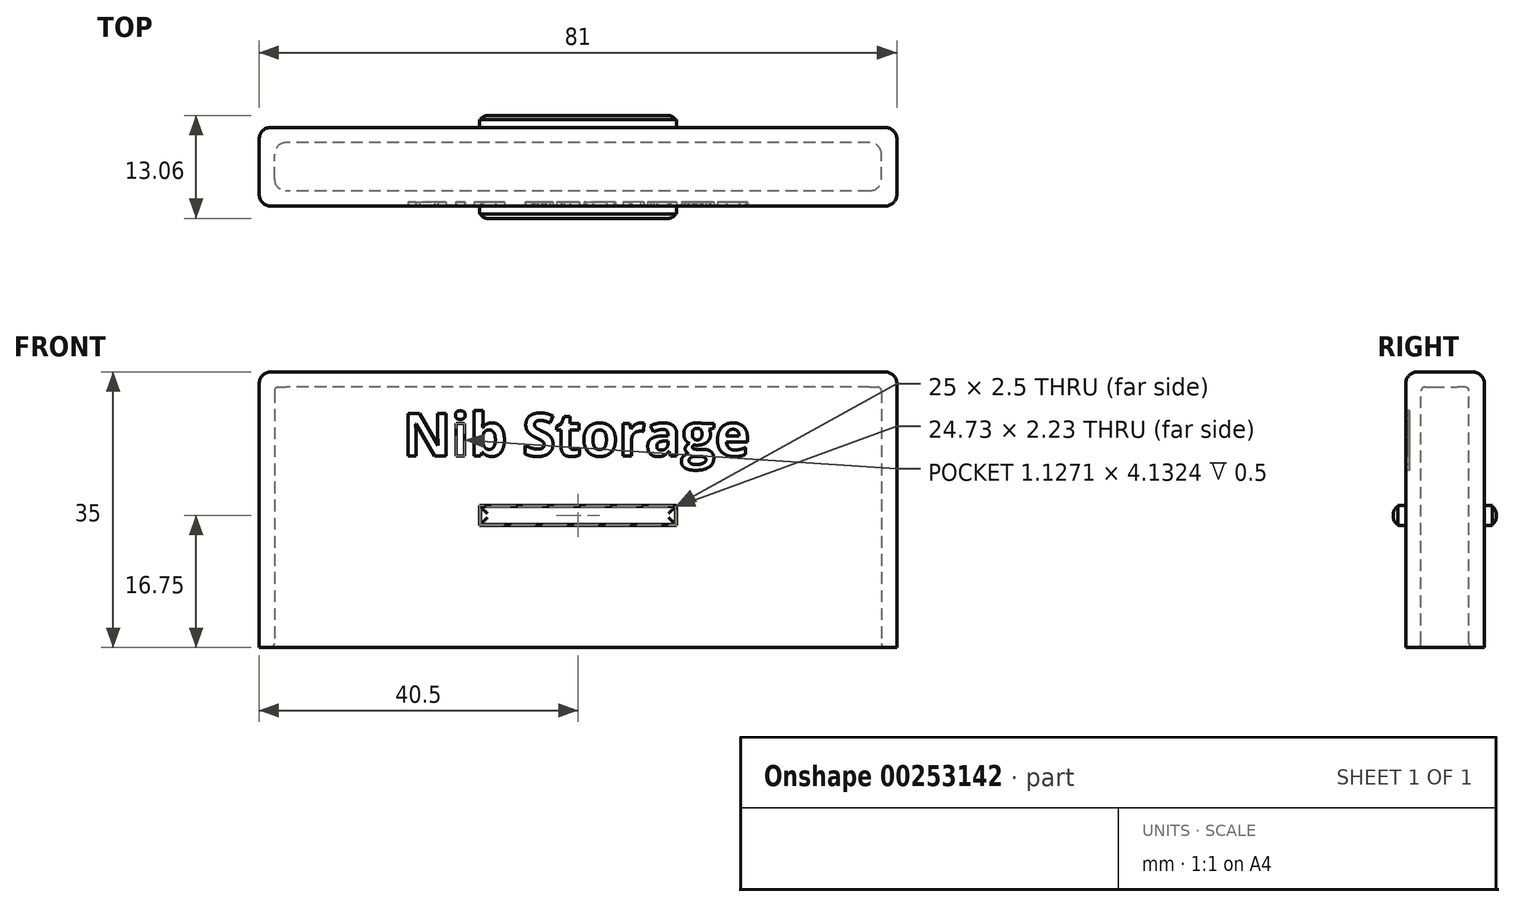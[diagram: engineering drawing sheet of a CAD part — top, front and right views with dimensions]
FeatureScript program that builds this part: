
annotation { "Feature Type Name" : "Feature", "Feature Type Description" : "" }
export const myFeature = defineFeature(function(context is Context, id is Id, definition is map)
    precondition{}
    {
        {
            var Q0;
            Q0=qCreatedBy(makeId("Top.planeOp"),FACE);
            var sketch = newSketch(context, id + "F0", { "sketchPlane" : qUnion([Q0])});
            skLineSegment(sketch, "E0.bottom", {"start": v(40.5, -5) * mm, "end": v(-40.5, -5) * mm});
            skLineSegment(sketch, "E0.top", {"start": v(40.5, 5) * mm, "end": v(-40.5, 5) * mm});
            skLineSegment(sketch, "E0.left", {"start": v(40.5, -5) * mm, "end": v(40.5, 5) * mm});
            skLineSegment(sketch, "E0.right", {"start": v(-40.5, -5) * mm, "end": v(-40.5, 5) * mm});
            skPoint(sketch, "E0.middle", {"position": v(0, 0) * mm});
            skSolve(sketch);
        }
        {
            var Q0;
            Q0=qSketchRegion(id+"F0",true);
            extrude(context, id + "F1", {"entities" : qUnion([Q0]), "depth" : 35 * mm});
        }
        {
            var Q0;
            Q0=makeQuery(id+"F1.opExtrude","CAP_EDGE",EDGE,{"disambiguationData":[OSD([sQuery(id+"F0.wireOp",EDGE,"E0.top")])],"isStart":false});
            var Q1;
            Q1=makeQuery(id+"F1.opExtrude","CAP_EDGE",EDGE,{"disambiguationData":[OSD([sQuery(id+"F0.wireOp",EDGE,"E0.bottom")])],"isStart":false});
            var Q2;
            Q2=makeQuery(id+"F1.opExtrude","CAP_EDGE",EDGE,{"disambiguationData":[OSD([sQuery(id+"F0.wireOp",EDGE,"E0.right")])],"isStart":false});
            var Q3;
            Q3=makeQuery(id+"F1.opExtrude","CAP_EDGE",EDGE,{"disambiguationData":[OSD([sQuery(id+"F0.wireOp",EDGE,"E0.left")])],"isStart":false});
            var Q4;
            Q4=makeQuery(id+"F1.opExtrude","SWEPT_EDGE",EDGE,{"disambiguationData":[OSD([sQuery(id+"F0.wireOp",EDGE,"E0.top"),sQuery(id+"F0.wireOp",EDGE,"E0.right")])]});
            var Q5;
            Q5=makeQuery(id+"F1.opExtrude","SWEPT_EDGE",EDGE,{"disambiguationData":[OSD([sQuery(id+"F0.wireOp",EDGE,"E0.bottom"),sQuery(id+"F0.wireOp",EDGE,"E0.right")])]});
            var Q6;
            Q6=makeQuery(id+"F1.opExtrude","SWEPT_EDGE",EDGE,{"disambiguationData":[OSD([sQuery(id+"F0.wireOp",EDGE,"E0.top"),sQuery(id+"F0.wireOp",EDGE,"E0.left")])]});
            var Q7;
            Q7=makeQuery(id+"F1.opExtrude","SWEPT_EDGE",EDGE,{"disambiguationData":[OSD([sQuery(id+"F0.wireOp",EDGE,"E0.bottom"),sQuery(id+"F0.wireOp",EDGE,"E0.left")])]});
            fillet(context, id + "F2", {"entities" : qUnion([Q0, Q1, Q2, Q3, Q4, Q5, Q6, Q7]), "radius" : 1.5 * mm, "tangentPropagation" : true, "allowEdgeOverflow" : false});
        }
        {
            var Q0;
            Q0=makeQuery(id+"F1.opExtrude","CAP_FACE",FACE,{"disambiguationData":[OSD([sQuery(id+"F0.wireOp",EDGE,"E0.bottom"),sQuery(id+"F0.wireOp",EDGE,"E0.top"),sQuery(id+"F0.wireOp",EDGE,"E0.left"),sQuery(id+"F0.wireOp",EDGE,"E0.right")])],"isStart":true});
            shell(context, id + "F3", {"entities" : qUnion([Q0]), "thickness" : 1.94 * mm});
        }
        {
            var Q0;
            Q0=makeQuery(id+"F3.opShell","OFFSET_EDGE",EDGE,{"disambiguationData":[OSD([sQuery(id+"F0.wireOp",EDGE,"E0.top"),sQuery(id+"F0.wireOp",EDGE,"E0.left")])]});
            var Q1;
            Q1=makeQuery(id+"F3.opShell","OFFSET_EDGE",EDGE,{"disambiguationData":[OSD([sQuery(id+"F0.wireOp",EDGE,"E0.bottom"),sQuery(id+"F0.wireOp",EDGE,"E0.left")])]});
            var Q2;
            Q2=makeQuery(id+"F3.opShell","OFFSET_EDGE",EDGE,{"disambiguationData":[OSD([sQuery(id+"F0.wireOp",EDGE,"E0.bottom"),sQuery(id+"F0.wireOp",EDGE,"E0.right")])]});
            var Q3;
            Q3=makeQuery(id+"F3.opShell","OFFSET_EDGE",EDGE,{"disambiguationData":[OSD([sQuery(id+"F0.wireOp",EDGE,"E0.top"),sQuery(id+"F0.wireOp",EDGE,"E0.right")])]});
            fillet(context, id + "F4", {"entities" : qUnion([Q0, Q1, Q2, Q3]), "radius" : 1.5 * mm, "tangentPropagation" : true, "allowEdgeOverflow" : false});
        }
        {
            var Q0;
            Q0=makeQuery(id+"F1.opExtrude","SWEPT_FACE",FACE,{"disambiguationData":[OSD([sQuery(id+"F0.wireOp",EDGE,"E0.bottom")])]});
            var sketch = newSketch(context, id + "F5", { "sketchPlane" : qUnion([Q0])});
            skLineSegment(sketch, "E1", {"start": v(39, 16.75) * mm, "end": v(-39, 16.75) * mm, "construction": true});
            skLineSegment(sketch, "E2", {"start": v(0, 33.5) * mm, "end": v(0, 0) * mm, "construction": true});
            skLineSegment(sketch, "E3.bottom", {"start": v(-12.5, 18) * mm, "end": v(12.5, 18) * mm});
            skLineSegment(sketch, "E3.top", {"start": v(-12.5, 15.5) * mm, "end": v(12.5, 15.5) * mm});
            skLineSegment(sketch, "E3.left", {"start": v(-12.5, 18) * mm, "end": v(-12.5, 15.5) * mm});
            skLineSegment(sketch, "E3.right", {"start": v(12.5, 18) * mm, "end": v(12.5, 15.5) * mm});
            skPoint(sketch, "E3.middle", {"position": v(0, 16.75) * mm});
            skLineSegment(sketch, "E4", {"start": v(-39, 8.04) * mm, "end": v(39, 8.04) * mm, "construction": true});
            skSolve(sketch);
        }
        {
            var Q0;
            Q0=qSketchRegion(id+"F5",true);
            extrude(context, id + "F6", {"entities" : qUnion([Q0]), "operationType" : NewBodyOperationType.ADD, "depth" : 1.56 * mm});
        }
        {
            var Q0;
            Q0=makeQuery(id+"F6.opExtrude","CAP_EDGE",EDGE,{"disambiguationData":[OSD([sQuery(id+"F5.wireOp",EDGE,"E3.bottom")])],"isStart":false});
            var Q1;
            Q1=makeQuery(id+"F6.opExtrude","CAP_EDGE",EDGE,{"disambiguationData":[OSD([sQuery(id+"F5.wireOp",EDGE,"E3.right")])],"isStart":false});
            var Q2;
            Q2=makeQuery(id+"F6.opExtrude","CAP_EDGE",EDGE,{"disambiguationData":[OSD([sQuery(id+"F5.wireOp",EDGE,"E3.top")])],"isStart":false});
            var Q3;
            Q3=makeQuery(id+"F6.opExtrude","CAP_EDGE",EDGE,{"disambiguationData":[OSD([sQuery(id+"F5.wireOp",EDGE,"E3.left")])],"isStart":false});
            var Q4;
            Q4=makeQuery(id+"F6.opExtrude","CAP_EDGE",EDGE,{"disambiguationData":[OSD([sQuery(id+"F5.wireOp",EDGE,"PPb5qhu8-9LVF-MKHu-zQhD-LhnvQhcufIGx.top")])],"isStart":false});
            var Q5;
            Q5=makeQuery(id+"F6.opExtrude","CAP_EDGE",EDGE,{"disambiguationData":[OSD([sQuery(id+"F5.wireOp",EDGE,"PPb5qhu8-9LVF-MKHu-zQhD-LhnvQhcufIGx.left")])],"isStart":false});
            var Q6;
            Q6=makeQuery(id+"F6.opExtrude","CAP_EDGE",EDGE,{"disambiguationData":[OSD([sQuery(id+"F5.wireOp",EDGE,"PPb5qhu8-9LVF-MKHu-zQhD-LhnvQhcufIGx.right")])],"isStart":false});
            var Q7;
            Q7=makeQuery(id+"F6.opExtrude","CAP_EDGE",EDGE,{"disambiguationData":[OSD([sQuery(id+"F5.wireOp",EDGE,"RZCc3H5M-QmGw-o7o6-KQUz-1ymlxaeq3NIj.left")])],"isStart":false});
            var Q8;
            Q8=makeQuery(id+"F6.opExtrude","CAP_EDGE",EDGE,{"disambiguationData":[OSD([sQuery(id+"F5.wireOp",EDGE,"RZCc3H5M-QmGw-o7o6-KQUz-1ymlxaeq3NIj.bottom")])],"isStart":false});
            var Q9;
            Q9=makeQuery(id+"F6.opExtrude","CAP_EDGE",EDGE,{"disambiguationData":[OSD([sQuery(id+"F5.wireOp",EDGE,"RZCc3H5M-QmGw-o7o6-KQUz-1ymlxaeq3NIj.right")])],"isStart":false});
            var Q10;
            Q10=makeQuery(id+"F6.opExtrude","CAP_EDGE",EDGE,{"disambiguationData":[OSD([sQuery(id+"F5.wireOp",EDGE,"RZCc3H5M-QmGw-o7o6-KQUz-1ymlxaeq3NIj.top")])],"isStart":false});
            var Q11;
            Q11=makeQuery(id+"F6.opExtrude","CAP_EDGE",EDGE,{"disambiguationData":[OSD([sQuery(id+"F5.wireOp",EDGE,"PPb5qhu8-9LVF-MKHu-zQhD-LhnvQhcufIGx.bottom")])],"isStart":false});
            fillet(context, id + "F7", {"entities" : qUnion([Q0, Q1, Q2, Q3, Q4, Q5, Q6, Q7, Q8, Q9, Q10, Q11]), "radius" : 1 * mm, "tangentPropagation" : true, "allowEdgeOverflow" : false});
        }
        {
            var Q0;
            Q0=makeQuery(id+"F1.opExtrude","SWEPT_FACE",FACE,{"disambiguationData":[OSD([sQuery(id+"F0.wireOp",EDGE,"E0.top")])]});
            var sketch = newSketch(context, id + "F8", { "sketchPlane" : qUnion([Q0])});
            skLineSegment(sketch, "E5", {"start": v(-39, 16.75) * mm, "end": v(-34.64, 16.75) * mm, "construction": true});
            skPoint(sketch, "E5.endSnap0", {"position": v(-39, 16.75) * mm});
            skLineSegment(sketch, "E6", {"start": v(39, 16.75) * mm, "end": v(-39, 16.75) * mm, "construction": true});
            skLineSegment(sketch, "E7", {"start": v(0, 33.5) * mm, "end": v(0, 0) * mm, "construction": true});
            skLineSegment(sketch, "E8.bottom", {"start": v(-12.5, 18) * mm, "end": v(12.5, 18) * mm});
            skLineSegment(sketch, "E8.top", {"start": v(-12.5, 15.5) * mm, "end": v(12.5, 15.5) * mm});
            skLineSegment(sketch, "E8.left", {"start": v(-12.5, 18) * mm, "end": v(-12.5, 15.5) * mm});
            skLineSegment(sketch, "E8.right", {"start": v(12.5, 18) * mm, "end": v(12.5, 15.5) * mm});
            skPoint(sketch, "E8.middle", {"position": v(0, 16.75) * mm});
            skLineSegment(sketch, "E9", {"start": v(39, 8.8) * mm, "end": v(-39, 8.8) * mm, "construction": true});
            skSolve(sketch);
        }
        {
            var Q0;
            Q0=qSketchRegion(id+"F8",true);
            extrude(context, id + "F9", {"entities" : qUnion([Q0]), "operationType" : NewBodyOperationType.ADD, "depth" : 1.5 * mm});
        }
        {
            var Q0;
            Q0=makeQuery(id+"F9.opExtrude","CAP_EDGE",EDGE,{"disambiguationData":[OSD([sQuery(id+"F8.wireOp",EDGE,"E8.bottom")])],"isStart":false});
            var Q1;
            Q1=makeQuery(id+"F9.opExtrude","CAP_EDGE",EDGE,{"disambiguationData":[OSD([sQuery(id+"F8.wireOp",EDGE,"E8.top")])],"isStart":false});
            var Q2;
            Q2=makeQuery(id+"F9.opExtrude","CAP_EDGE",EDGE,{"disambiguationData":[OSD([sQuery(id+"F8.wireOp",EDGE,"E8.left")])],"isStart":false});
            var Q3;
            Q3=makeQuery(id+"F9.opExtrude","CAP_EDGE",EDGE,{"disambiguationData":[OSD([sQuery(id+"F8.wireOp",EDGE,"E8.right")])],"isStart":false});
            var Q4;
            Q4=makeQuery(id+"F9.opExtrude","CAP_EDGE",EDGE,{"disambiguationData":[OSD([sQuery(id+"F8.wireOp",EDGE,"s05gpshp-pCmh-c7mK-lPRz-FeS4k08mUUMQ.top")])],"isStart":false});
            var Q5;
            Q5=makeQuery(id+"F9.opExtrude","CAP_EDGE",EDGE,{"disambiguationData":[OSD([sQuery(id+"F8.wireOp",EDGE,"s05gpshp-pCmh-c7mK-lPRz-FeS4k08mUUMQ.bottom")])],"isStart":false});
            var Q6;
            Q6=makeQuery(id+"F9.opExtrude","CAP_EDGE",EDGE,{"disambiguationData":[OSD([sQuery(id+"F8.wireOp",EDGE,"s05gpshp-pCmh-c7mK-lPRz-FeS4k08mUUMQ.right")])],"isStart":false});
            var Q7;
            Q7=makeQuery(id+"F9.opExtrude","CAP_FACE",FACE,{"disambiguationData":[OSD([sQuery(id+"F8.wireOp",EDGE,"s05gpshp-pCmh-c7mK-lPRz-FeS4k08mUUMQ.bottom"),sQuery(id+"F8.wireOp",EDGE,"s05gpshp-pCmh-c7mK-lPRz-FeS4k08mUUMQ.top"),sQuery(id+"F8.wireOp",EDGE,"s05gpshp-pCmh-c7mK-lPRz-FeS4k08mUUMQ.left"),sQuery(id+"F8.wireOp",EDGE,"s05gpshp-pCmh-c7mK-lPRz-FeS4k08mUUMQ.right")])],"isStart":false});
            var Q8;
            Q8=makeQuery(id+"F9.opExtrude","CAP_EDGE",EDGE,{"disambiguationData":[OSD([sQuery(id+"F8.wireOp",EDGE,"PnnPUle7-DzCa-uMxP-33LW-th4631gfkKbC.left")])],"isStart":false});
            var Q9;
            Q9=makeQuery(id+"F9.opExtrude","CAP_EDGE",EDGE,{"disambiguationData":[OSD([sQuery(id+"F8.wireOp",EDGE,"PnnPUle7-DzCa-uMxP-33LW-th4631gfkKbC.right")])],"isStart":false});
            var Q10;
            Q10=makeQuery(id+"F9.opExtrude","CAP_EDGE",EDGE,{"disambiguationData":[OSD([sQuery(id+"F8.wireOp",EDGE,"PnnPUle7-DzCa-uMxP-33LW-th4631gfkKbC.top")])],"isStart":false});
            var Q11;
            Q11=makeQuery(id+"F9.opExtrude","CAP_EDGE",EDGE,{"disambiguationData":[OSD([sQuery(id+"F8.wireOp",EDGE,"PnnPUle7-DzCa-uMxP-33LW-th4631gfkKbC.bottom")])],"isStart":false});
            fillet(context, id + "F10", {"entities" : qUnion([Q0, Q1, Q2, Q3, Q4, Q5, Q6, Q7, Q8, Q9, Q10, Q11]), "radius" : 1 * mm, "tangentPropagation" : true, "allowEdgeOverflow" : false});
        }
        {
            var Q0;
            Q0=makeQuery(id+"F3.opShell","OFFSET_FACE",FACE,{"disambiguationData":[OSD([sQuery(id+"F0.wireOp",EDGE,"E0.left")])]});
            fillet(context, id + "F11", {"entities" : qUnion([Q0]), "radius" : .5 * mm, "tangentPropagation" : true, "allowEdgeOverflow" : false});
        }
        {
            var Q0;
            Q0=qSketchRegion(id+"F8",true);
            extrude(context, id + "F12", {"entities" : qUnion([Q0]), "operationType" : NewBodyOperationType.ADD, "depth" : 1 * mm});
        }
        {
            var Q0;
            Q0=qSketchRegion(id+"F5",true);
            extrude(context, id + "F13", {"entities" : qUnion([Q0]), "operationType" : NewBodyOperationType.ADD, "depth" : 1 * mm});
        }
        {
            var Q0;
            Q0=makeQuery(id+"F5.imprint","IMPRINT",FACE,{"disambiguationData":[TD([[makeQuery(id+"F5.imprint","IMPRINT",EDGE,{"derivedFrom":sQuery(id+"F5.wireOp",EDGE,"E3.bottom")}),1.0]])]});
            var sketch = newSketch(context, id + "F14", { "sketchPlane" : qUnion([Q0])});
            skText(sketch, "E10", { "text": "Nib Storage\n", "fontName": "OpenSans-Bold.ttf"});
            const initialGuessF14  = {"E10": [-0.02226, 0.02431, 1, 0, 0.00545]};
            skSetInitialGuess(sketch, initialGuessF14);
            skSolve(sketch);
        }
        {
            var Q0;
            Q0=qSketchRegion(id+"F14",true);
            extrude(context, id + "F15", {"entities" : qUnion([Q0]), "operationType" : NewBodyOperationType.REMOVE, "oppositeDirection" : true, "depth" : .5 * mm});
        }
    });
